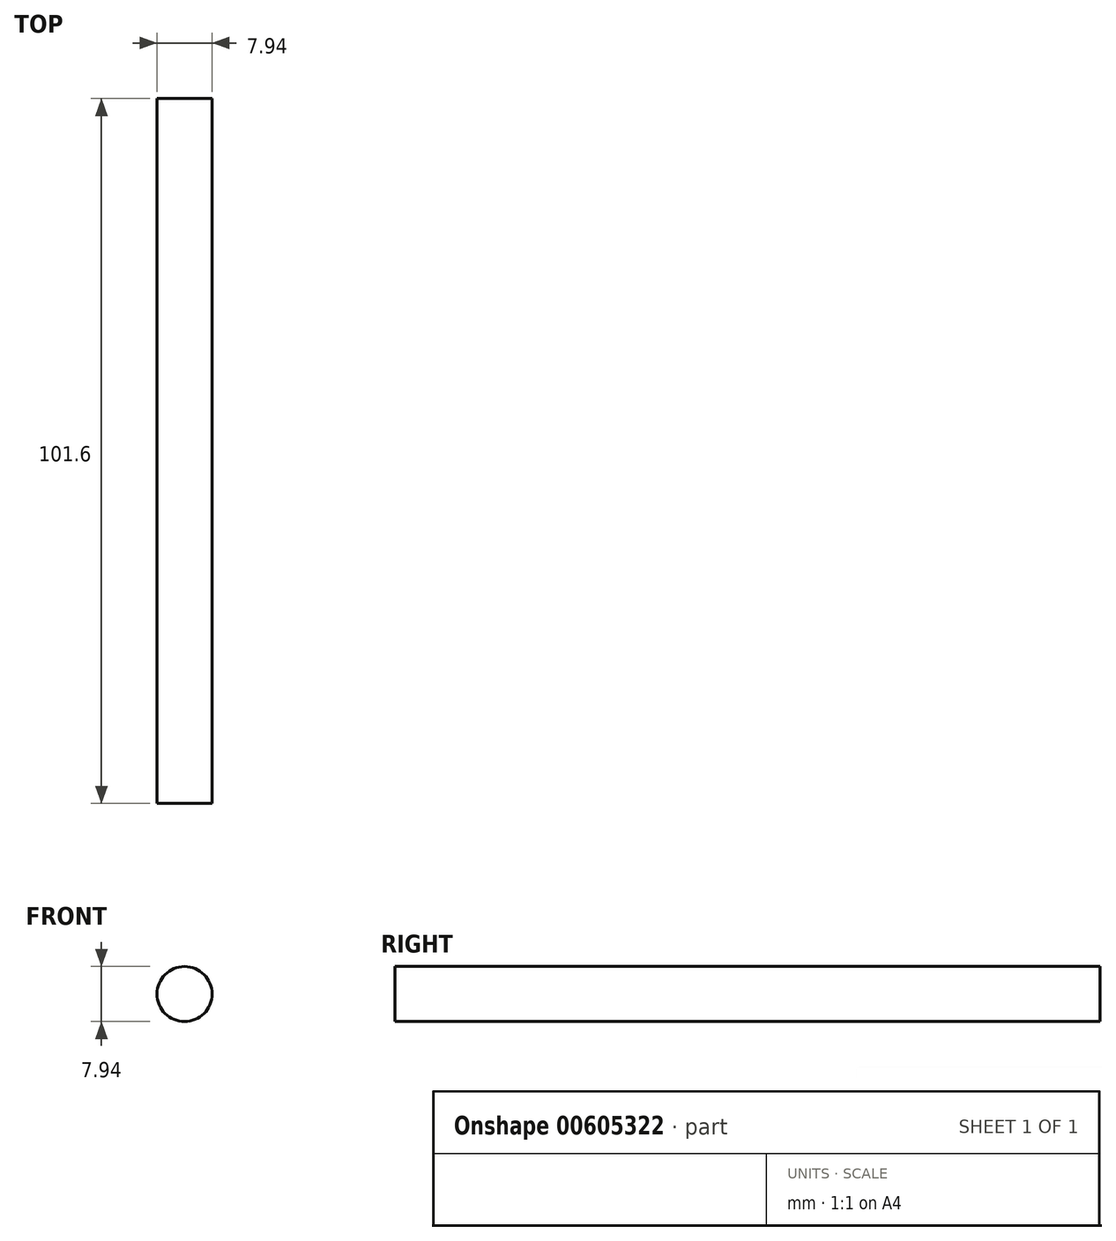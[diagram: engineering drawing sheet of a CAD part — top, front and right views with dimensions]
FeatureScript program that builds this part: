
annotation { "Feature Type Name" : "Feature", "Feature Type Description" : "" }
export const myFeature = defineFeature(function(context is Context, id is Id, definition is map)
    precondition{}
    {
        {
            var Q0;
            Q0=qCreatedBy(makeId("Front.planeOp"),FACE);
            var sketch = newSketch(context, id + "F0", { "sketchPlane" : qUnion([Q0])});
            skCircle(sketch, "E0", {"center": v(0, 0) * mm, "radius": 3.97 * mm});
            skSolve(sketch);
        }
        {
            var Q0;
            Q0 = qSketchRegion(id + "F0", true);
            extrude(context, id + "F1", {"entities" : qUnion([Q0]), "depth" : 101.6 * mm, "offsetDistance" : 25 * mm});
        }
    });
